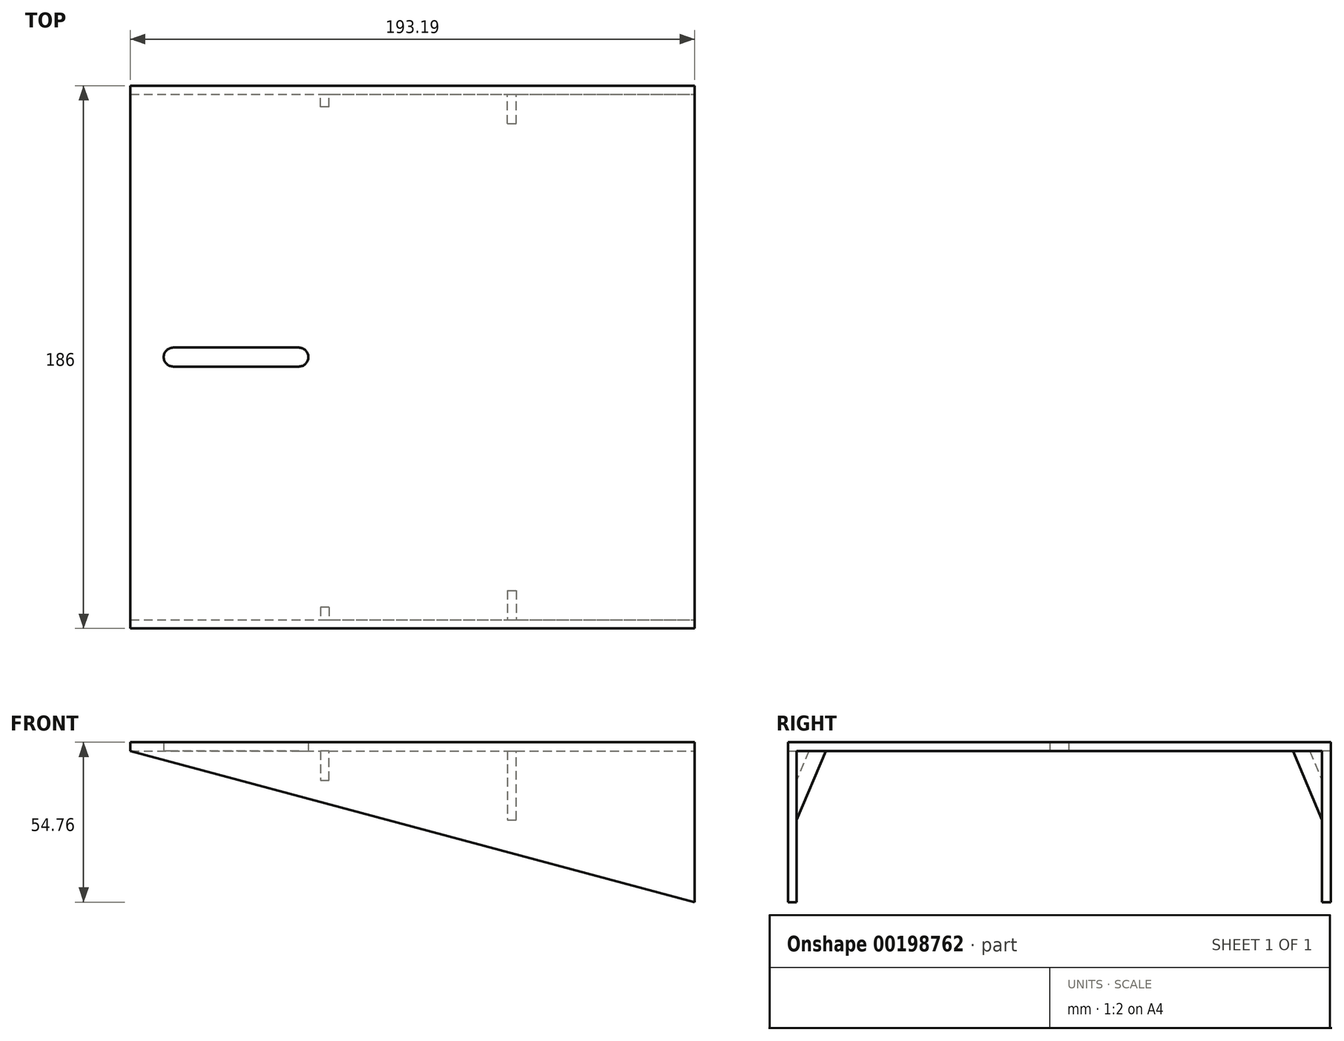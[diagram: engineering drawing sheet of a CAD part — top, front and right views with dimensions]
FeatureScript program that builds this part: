
annotation { "Feature Type Name" : "Feature", "Feature Type Description" : "" }
export const myFeature = defineFeature(function(context is Context, id is Id, definition is map)
    precondition{}
    {
        {
            var Q0;
            Q0=qCreatedBy(makeId("Front.planeOp"),FACE);
            var sketch = newSketch(context, id + "F0", { "sketchPlane" : qUnion([Q0])});
            skLineSegment(sketch, "E0", {"start": v(-150.69, 51.76) * mm, "end": v(42.5, 0) * mm});
            skLineSegment(sketch, "E1", {"start": v(-150.69, 51.76) * mm, "end": v(42.5, 51.76) * mm});
            skLineSegment(sketch, "E2", {"start": v(42.5, 0) * mm, "end": v(42.5, 51.76) * mm});
            skLineSegment(sketch, "E3.0", {"start": v(-150.69, 54.76) * mm, "end": v(42.5, 54.76) * mm});
            skLineSegment(sketch, "E4", {"start": v(42.5, 54.76) * mm, "end": v(42.5, 51.76) * mm});
            skLineSegment(sketch, "E5", {"start": v(-150.69, 54.76) * mm, "end": v(-150.69, 51.76) * mm});
            skLineSegment(sketch, "E6", {"start": v(0, 0) * mm, "end": v(-189.3, 0) * mm});
            skLineSegment(sketch, "E7", {"start": v(-150.69, 51.76) * mm, "end": v(-150.69, 0) * mm});
            skLineSegment(sketch, "E8", {"start": v(42.5, 51.76) * mm, "end": v(-85.63, 51.76) * mm});
            skLineSegment(sketch, "E9", {"start": v(-85.63, 51.76) * mm, "end": v(-85.63, 41.76) * mm});
            skLineSegment(sketch, "E10", {"start": v(-85.63, 41.76) * mm, "end": v(-82.63, 41.76) * mm});
            skLineSegment(sketch, "E11", {"start": v(-82.63, 41.76) * mm, "end": v(-82.63, 51.76) * mm});
            skLineSegment(sketch, "E12", {"start": v(42.5, 51.76) * mm, "end": v(-21.56, 51.76) * mm});
            skLineSegment(sketch, "E13", {"start": v(-21.56, 51.76) * mm, "end": v(-21.56, 28.17) * mm});
            skLineSegment(sketch, "E14", {"start": v(-21.56, 28.17) * mm, "end": v(-18.56, 28.17) * mm});
            skLineSegment(sketch, "E15", {"start": v(-18.56, 28.17) * mm, "end": v(-18.56, 51.76) * mm});
            skSolve(sketch);
        }
        {
            var Q0;
            Q0 = qSketchRegion(id + "F0", true);
            var Q1;
            {var subQ0=sQuery(id+"F0.wireOp",EDGE,"E13");Q1=makeQuery(id+"F0.imprint","IMPRINT",FACE,{"disambiguationData":[TD([[makeQuery(id+"F0.imprint","IMPRINT",EDGE,{"derivedFrom":subQ0}),1.0]])]});}
            var Q2;
            {var subQ0=sQuery(id+"F0.wireOp",EDGE,"E9");Q2=makeQuery(id+"F0.imprint","IMPRINT",FACE,{"disambiguationData":[TD([[makeQuery(id+"F0.imprint","IMPRINT",EDGE,{"derivedFrom":subQ0}),1.0]])]});}
            extrude(context, id + "F1", {"entities" : qUnion([Q0, Q1, Q2]), "depth" : 3 * mm, "offsetDistance" : 25.4 * mm});
        }
        {
            var Q0;
            Q0=makeQuery(id+"F0.imprint","IMPRINT",FACE,{"disambiguationData":[TD([[makeQuery(id+"F0.imprint","IMPRINT",EDGE,{"derivedFrom":sQuery(id+"F0.wireOp",EDGE,"E1")}),1.0]])]});
            extrude(context, id + "F2", {"entities" : qUnion([Q0]), "operationType" : NewBodyOperationType.ADD, "oppositeDirection" : true, "depth" : 90 * mm});
        }
        {
            var Q0;
            Q0=qCreatedBy(makeId("Top.planeOp"),FACE);
            var sketch = newSketch(context, id + "F3", { "sketchPlane" : qUnion([Q0])});
            skLineSegment(sketch, "E16", {"start": v(0, 0) * mm, "end": v(0, 90) * mm});
            skLineSegment(sketch, "E17", {"start": v(0, 90) * mm, "end": v(-124.46, 90) * mm});
            skLineSegment(sketch, "E18", {"start": v(-124.46, 90) * mm, "end": v(-136.04, 90) * mm});
            skCircle(sketch, "E19", {"center": v(-136.04, 90) * mm, "radius": 3.25 * mm});
            skLineSegment(sketch, "E20", {"start": v(0, 90) * mm, "end": v(-92.99, 90) * mm});
            skCircle(sketch, "E21", {"center": v(-92.99, 90) * mm, "radius": 3.25 * mm});
            skLineSegment(sketch, "E22", {"start": v(-92.99, 93.25) * mm, "end": v(-136.04, 93.25) * mm});
            skLineSegment(sketch, "E23", {"start": v(-92.99, 86.75) * mm, "end": v(-136.04, 86.75) * mm});
            skSolve(sketch);
        }
        {
            var Q0;
            {var subQ0=sQuery(id+"F0.wireOp",EDGE,"E13");Q0=makeQuery(id+"F0.imprint","IMPRINT",FACE,{"disambiguationData":[TD([[makeQuery(id+"F0.imprint","IMPRINT",EDGE,{"derivedFrom":subQ0}),1.0]])]});}
            var Q1;
            {var subQ0=sQuery(id+"F0.wireOp",EDGE,"E9");Q1=makeQuery(id+"F0.imprint","IMPRINT",FACE,{"disambiguationData":[TD([[makeQuery(id+"F0.imprint","IMPRINT",EDGE,{"derivedFrom":subQ0}),1.0]])]});}
            extrude(context, id + "F4", {"entities" : qUnion([Q0, Q1]), "oppositeDirection" : true, "depth" : 10 * mm});
        }
        {
            var Q0;
            Q0=makeQuery(id+"F4.opExtrude","CAP_EDGE",EDGE,{"disambiguationData":[OSD([sQuery(id+"F0.wireOp",EDGE,"E14")])],"isStart":false});
            var Q1;
            Q1=makeQuery(id+"F4.opExtrude","CAP_EDGE",EDGE,{"disambiguationData":[OSD([sQuery(id+"F0.wireOp",EDGE,"E10")])],"isStart":false});
            chamfer(context, id + "F5", {"entities" : qUnion([Q0, Q1]), "chamferType" : ChamferType.TWO_OFFSETS, "width1" : 10 * mm, "oppositeDirection" : false, "width2" : 23.6 * mm, "tangentPropagation" : true});
        }
        {
            var Q0;
            Q0=makeQuery(id+"F1.opExtrude","SWEPT_BODY",BODY,{"disambiguationData":[OSD([sQuery(id+"F0.wireOp",EDGE,"E0"),sQuery(id+"F0.wireOp",EDGE,"E2"),sQuery(id+"F0.wireOp",EDGE,"E3.0"),sQuery(id+"F0.wireOp",EDGE,"E4"),sQuery(id+"F0.wireOp",EDGE,"E5")])]});
            var Q1;
            Q1=makeQuery(id+"F4.opExtrude","SWEPT_BODY",BODY,{"disambiguationData":[OSD([sQuery(id+"F0.wireOp",EDGE,"E12"),sQuery(id+"F0.wireOp",EDGE,"E13"),sQuery(id+"F0.wireOp",EDGE,"E14"),sQuery(id+"F0.wireOp",EDGE,"E15")])]});
            var Q2;
            Q2=makeQuery(id+"F4.opExtrude","SWEPT_BODY",BODY,{"disambiguationData":[OSD([sQuery(id+"F0.wireOp",EDGE,"E8"),sQuery(id+"F0.wireOp",EDGE,"E9"),sQuery(id+"F0.wireOp",EDGE,"E10"),sQuery(id+"F0.wireOp",EDGE,"E11")])]});
            var Q3;
            Q3=makeQuery(id+"F2.opExtrude","CAP_FACE",FACE,{"disambiguationData":[OSD([sQuery(id+"F0.wireOp",EDGE,"E1"),sQuery(id+"F0.wireOp",EDGE,"E3.0"),sQuery(id+"F0.wireOp",EDGE,"E4"),sQuery(id+"F0.wireOp",EDGE,"E5")])],"isStart":false});
            mirror(context, id + "F6", {"operationType" : NewBodyOperationType.ADD, "entities" : qUnion([Q0, Q1, Q2]), "mirrorPlane" : qUnion([Q3])});
        }
        {
            var Q0;
            Q0 = qSketchRegion(id + "F3", true);
            var Q1;
            {var subQ0=sQuery(id+"F0.wireOp",EDGE,"E3.0");var subQ1=makeQuery(id+"F2.boolean.opBoolean","MERGE",FACE,{"derivedFrom":[makeQuery(id+"F1.opExtrude","SWEPT_FACE",FACE,{"disambiguationData":[OSD([subQ0])]}),makeQuery(id+"F2.opExtrude","SWEPT_FACE",FACE,{"disambiguationData":[OSD([subQ0])]})]});Q1=makeQuery(id+"F6.boolean.opBoolean","MERGE",FACE,{"derivedFrom":[subQ1,makeQuery(id+"F6.opPattern","COPY",FACE,{"derivedFrom":subQ1,"instanceName":"1"})]});}
            extrude(context, id + "F7", {"entities" : qUnion([Q0, Q1]), "operationType" : NewBodyOperationType.REMOVE, "depth" : 254 * mm});
        }
    });
